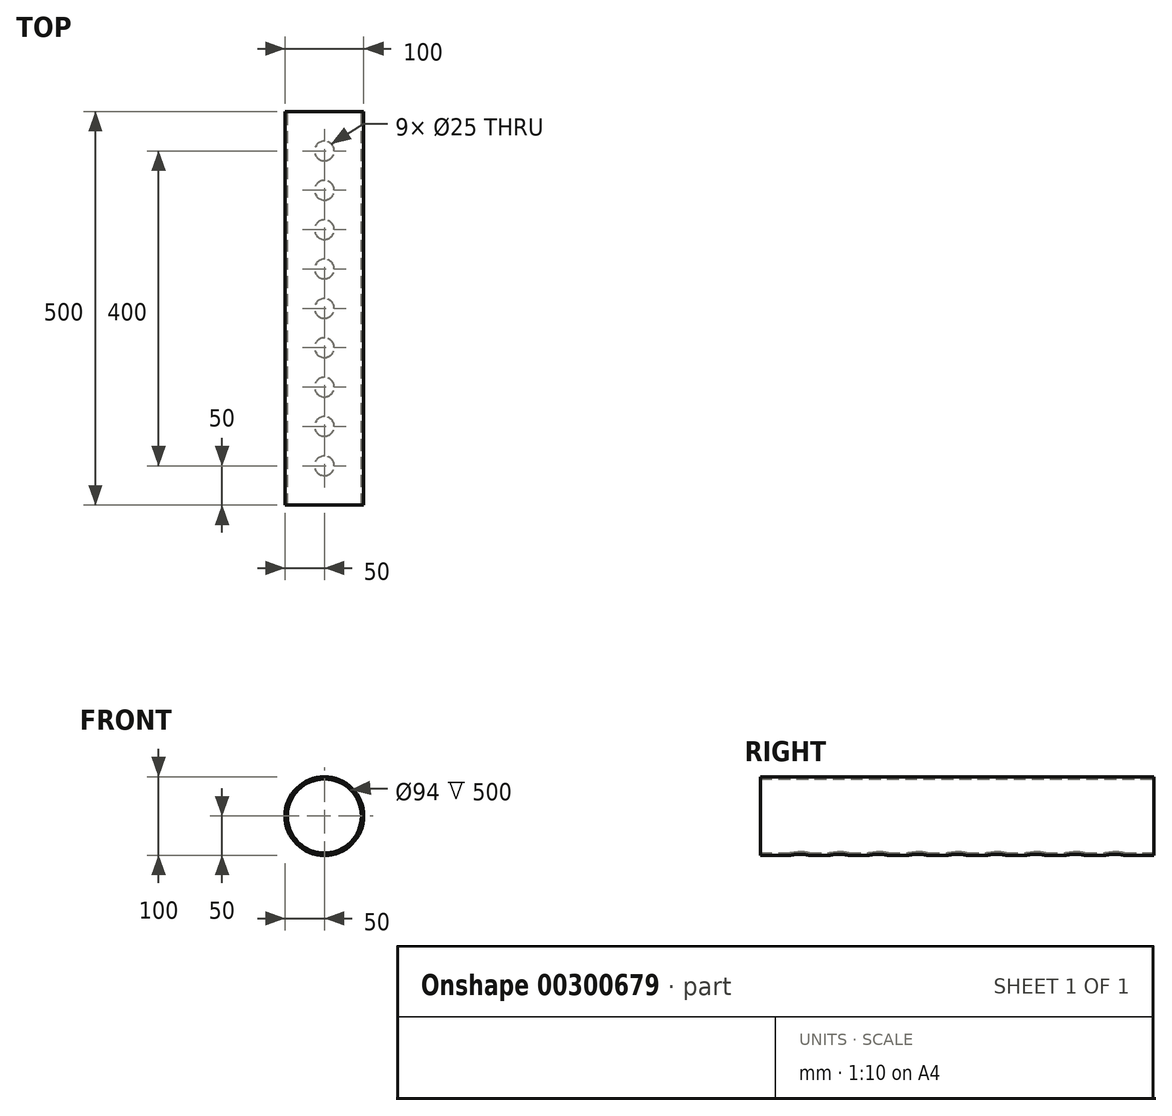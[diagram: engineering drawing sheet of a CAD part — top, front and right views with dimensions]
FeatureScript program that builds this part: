
annotation { "Feature Type Name" : "Feature", "Feature Type Description" : "" }
export const myFeature = defineFeature(function(context is Context, id is Id, definition is map)
    precondition{}
    {
        {
            var Q0;
            Q0=qCreatedBy(makeId("Front.planeOp"),FACE);
            var sketch = newSketch(context, id + "F0", { "sketchPlane" : qUnion([Q0])});
            skCircle(sketch, "E0", {"center": v(0, 0) * mm, "radius": 50 * mm});
            skCircle(sketch, "E1", {"center": v(0, 0) * mm, "radius": 47 * mm});
            skSolve(sketch);
        }
        {
            var Q0;
            Q0 = qSketchRegion(id + "F0", true);
            extrude(context, id + "F1", {"entities" : qUnion([Q0]), "depth" : 500 * mm});
        }
        {
            var Q0;
            Q0=qCreatedBy(makeId("Top.planeOp"),FACE);
            var sketch = newSketch(context, id + "F2", { "sketchPlane" : qUnion([Q0])});
            skCircle(sketch, "E2", {"center": v(0, -350) * mm, "radius": 12.5 * mm});
            skCircle(sketch, "E3", {"center": v(0, -300) * mm, "radius": 12.5 * mm});
            skCircle(sketch, "E4", {"center": v(0, -250) * mm, "radius": 12.5 * mm});
            skCircle(sketch, "E5", {"center": v(0, -150) * mm, "radius": 12.5 * mm});
            skCircle(sketch, "E6", {"center": v(0, -200) * mm, "radius": 12.5 * mm});
            skCircle(sketch, "E7", {"center": v(0, -400) * mm, "radius": 12.5 * mm});
            skCircle(sketch, "E8", {"center": v(0, -100) * mm, "radius": 12.5 * mm});
            skCircle(sketch, "E9", {"center": v(0, -50) * mm, "radius": 12.5 * mm});
            skCircle(sketch, "E10", {"center": v(0, -450) * mm, "radius": 12.5 * mm});
            skSolve(sketch);
        }
        {
            var Q0;
            Q0 = qSketchRegion(id + "F2", true);
            extrude(context, id + "F3", {"entities" : qUnion([Q0]), "operationType" : NewBodyOperationType.REMOVE, "oppositeDirection" : true, "depth" : 80 * mm});
        }
    });
